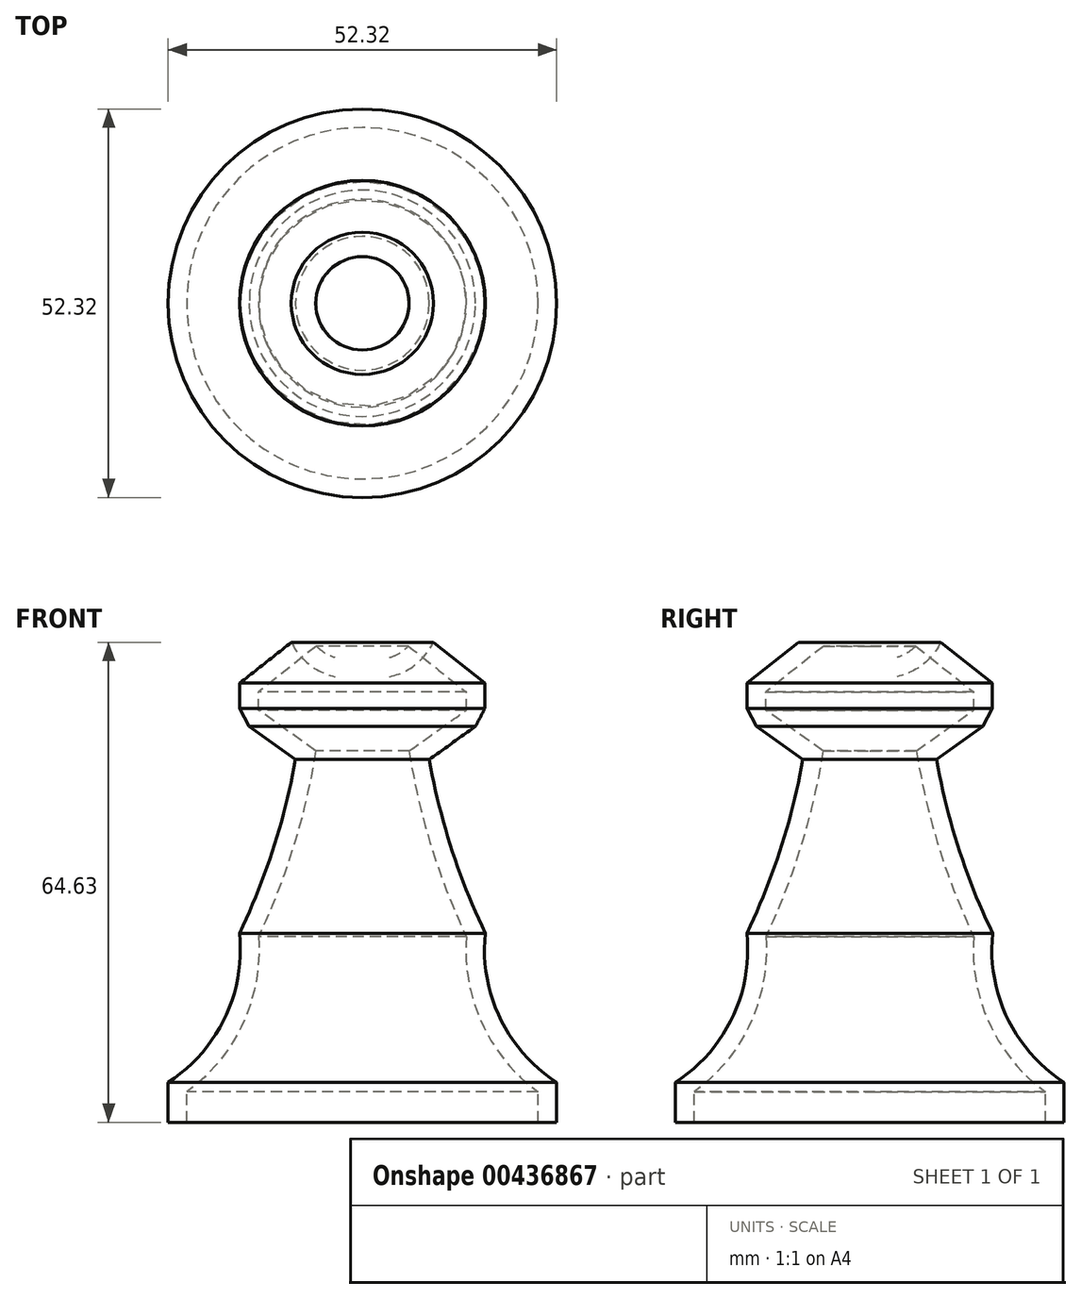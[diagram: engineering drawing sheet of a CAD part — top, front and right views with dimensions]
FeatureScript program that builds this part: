
annotation { "Feature Type Name" : "Feature", "Feature Type Description" : "" }
export const myFeature = defineFeature(function(context is Context, id is Id, definition is map)
    precondition{}
    {
        {
            var Q0;
            Q0=qCreatedBy(makeId("Front.planeOp"),FACE);
            var sketch = newSketch(context, id + "F0", { "sketchPlane" : qUnion([Q0])});
            skLineSegment(sketch, "E0", {"start": v(0, 50) * mm, "end": v(0, 0) * mm});
            skLineSegment(sketch, "E1", {"start": v(0, 0) * mm, "end": v(-25.32, 0) * mm});
            skLineSegment(sketch, "E2", {"start": v(-23.66, -0.42) * mm, "end": v(-23.66, 4.08) * mm});
            skLineSegment(sketch, "E3", {"start": v(-23.66, 4.08) * mm, "end": v(0, 4.08) * mm});
            skLineSegment(sketch, "E4", {"start": v(0, 4.08) * mm, "end": v(0, 25) * mm});
            skLineSegment(sketch, "E5", {"start": v(0, 25) * mm, "end": v(-14, 25) * mm});
            skArc(sketch, "E6", {"start": v(-23.66, 4.08) * mm, "mid": v(-16.12, 13.29) * mm, "end": v(-14, 25) * mm});
            skLineSegment(sketch, "E7", {"start": v(0, 50) * mm, "end": v(-6.29, 50) * mm});
            skArc(sketch, "E8", {"start": v(-14, 25) * mm, "mid": v(-9.25, 37.22) * mm, "end": v(-6.29, 50) * mm});
            skLineSegment(sketch, "E9", {"start": v(-6.29, 50) * mm, "end": v(-14, 55.5) * mm});
            skLineSegment(sketch, "E10", {"start": v(-14, 55.5) * mm, "end": v(0, 55.5) * mm});
            skLineSegment(sketch, "E11", {"start": v(-14, 55.5) * mm, "end": v(-14, 57.94) * mm});
            skLineSegment(sketch, "E12", {"start": v(-14, 57.94) * mm, "end": v(0, 57.94) * mm});
            skLineSegment(sketch, "E13", {"start": v(-14, 57.94) * mm, "end": v(-6.19, 64.13) * mm});
            skArc(sketch, "E14", {"start": v(0, 74.25) * mm, "mid": v(-7.05, 71.6) * mm, "end": v(-6.19, 64.13) * mm});
            skLineSegment(sketch, "E15", {"start": v(0, 50) * mm, "end": v(0, 74.25) * mm});
            skSolve(sketch);
        }
        {
            var Q0;
            Q0=makeQuery(id+"F0.imprint","IMPRINT",FACE,{"disambiguationData":[TD([[makeQuery(id+"F0.imprint","IMPRINT",EDGE,{"derivedFrom":sQuery(id+"F0.wireOp",EDGE,"E3")}),1.0]])]});
            var Q1;
            {var subQ0=sQuery(id+"F0.wireOp",EDGE,"E7");Q1=makeQuery(id+"F0.imprint","IMPRINT",FACE,{"disambiguationData":[TD([[makeQuery(id+"F0.imprint","IMPRINT",EDGE,{"derivedFrom":subQ0}),-1.0]])]});}
            var Q2;
            {var subQ2=sQuery(id+"F0.wireOp",EDGE,"E5");Q2=makeQuery(id+"F0.imprint","IMPRINT",FACE,{"disambiguationData":[TD([[makeQuery(id+"F0.imprint","IMPRINT",EDGE,{"derivedFrom":subQ2}),-1.0]])]});}
            var Q3;
            {var subQ3=sQuery(id+"F0.wireOp",EDGE,"E3");Q3=makeQuery(id+"F0.imprint","IMPRINT",FACE,{"disambiguationData":[TD([[makeQuery(id+"F0.imprint","IMPRINT",EDGE,{"derivedFrom":subQ3}),-1.0]])]});}
            var Q4;
            {var subQ0=sQuery(id+"F0.wireOp",EDGE,"E12");Q4=makeQuery(id+"F0.imprint","IMPRINT",FACE,{"disambiguationData":[TD([[makeQuery(id+"F0.imprint","IMPRINT",EDGE,{"derivedFrom":subQ0}),1.0]])]});}
            var Q5;
            {var subQ0=sQuery(id+"F0.wireOp",EDGE,"E10");Q5=makeQuery(id+"F0.imprint","IMPRINT",FACE,{"disambiguationData":[TD([[makeQuery(id+"F0.imprint","IMPRINT",EDGE,{"derivedFrom":subQ0}),1.0]])]});}
            var Q6;
            Q6=sQuery(id+"F0.wireOp",EDGE,"E0");
            revolve(context, id + "F1", {"entities" : qUnion([Q0, Q1, Q2, Q3, Q4, Q5]), "axis" : qUnion([Q6]), "revolveType" : RevolveType.FULL});
        }
        {
            var Q0;
            Q0=makeQuery(id+"F1.opRevolve","SWEPT_FACE",FACE,{"disambiguationData":[OSD([sQuery(id+"F0.wireOp",EDGE,"E1")])]});
            shell(context, id + "F2", {"entities" : qUnion([Q0]), "thickness" : 2.5 * mm, "oppositeDirection" : true});
        }
        {
            var Q0;
            Q0=makeQuery(id+"F1.opRevolve","SWEPT_EDGE",EDGE,{"disambiguationData":[OSD([sQuery(id+"F0.wireOp",EDGE,"E9"),sQuery(id+"F0.wireOp",EDGE,"E10"),sQuery(id+"F0.wireOp",EDGE,"E11")])]});
            chamfer(context, id + "F3", {"entities" : qUnion([Q0]), "width" : 3 * mm, "tangentPropagation" : true});
        }
    });
